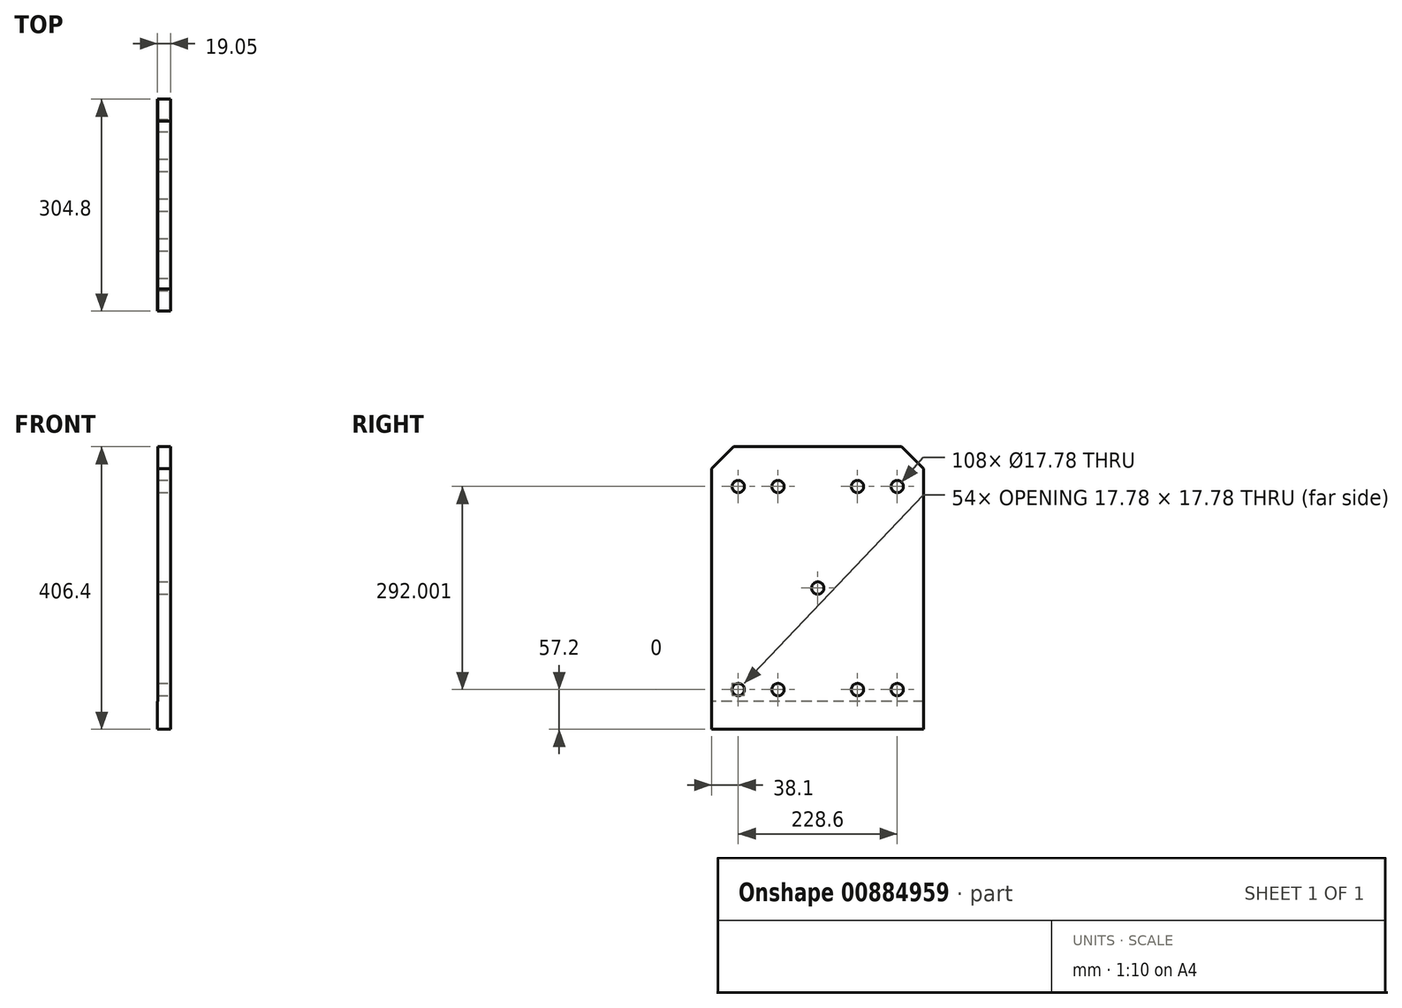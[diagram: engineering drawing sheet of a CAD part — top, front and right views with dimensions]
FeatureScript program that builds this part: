
annotation { "Feature Type Name" : "Feature", "Feature Type Description" : "" }
export const myFeature = defineFeature(function(context is Context, id is Id, definition is map)
    precondition{}
    {
        {
            var Q0;
            Q0=qCreatedBy(makeId("Right.planeOp"),FACE);
            var sketch = newSketch(context, id + "F0", { "sketchPlane" : qUnion([Q0])});
            skLineSegment(sketch, "E0.bottom", {"start": v(152.4, -203.2) * mm, "end": v(-152.4, -203.2) * mm});
            skLineSegment(sketch, "E0.top", {"start": v(120.65, 203.2) * mm, "end": v(-120.65, 203.2) * mm});
            skLineSegment(sketch, "E0.left", {"start": v(152.4, -203.2) * mm, "end": v(152.4, 171.45) * mm});
            skLineSegment(sketch, "E0.right", {"start": v(-152.4, -203.2) * mm, "end": v(-152.4, 171.45) * mm});
            skPoint(sketch, "E0.middle", {"position": v(0, 0) * mm});
            skPoint(sketch, "E1", {"position": v(152.4, 171.45) * mm});
            skLineSegment(sketch, "E2", {"start": v(152.4, 171.45) * mm, "end": v(120.65, 203.2) * mm});
            skPoint(sketch, "E3.orphan", {"position": v(152.4, 203.2) * mm});
            skLineSegment(sketch, "E4", {"start": v(152.4, 171.45) * mm, "end": v(-152.4, 171.45) * mm, "construction": true});
            skLineSegment(sketch, "E5", {"start": v(-152.4, 171.45) * mm, "end": v(-120.65, 203.2) * mm});
            skPoint(sketch, "E6.orphan", {"position": v(-152.4, 203.2) * mm});
            skSolve(sketch);
        }
        {
            var Q0;
            Q0 = qSketchRegion(id + "F0", true);
            extrude(context, id + "F1", {"entities" : qUnion([Q0]), "depth" : 19.05 * mm, "offsetDistance" : 25.4 * mm});
        }
        {
            var Q0;
            Q0=makeQuery(id+"F1.opExtrude","CAP_FACE",FACE,{"disambiguationData":[OSD([sQuery(id+"F0.wireOp",EDGE,"E0.bottom"),sQuery(id+"F0.wireOp",EDGE,"E0.top"),sQuery(id+"F0.wireOp",EDGE,"E0.left"),sQuery(id+"F0.wireOp",EDGE,"E0.right"),sQuery(id+"F0.wireOp",EDGE,"E2"),sQuery(id+"F0.wireOp",EDGE,"E5")])],"isStart":false});
            var sketch = newSketch(context, id + "F2", { "sketchPlane" : qUnion([Q0])});
            skLineSegment(sketch, "E7", {"start": v(0, -203.2) * mm, "end": v(0, 203.2) * mm, "construction": true});
            skPoint(sketch, "E8", {"position": v(0, -186.84) * mm});
            skCircle(sketch, "E9", {"center": v(-57.15, 146) * mm, "radius": 8.9 * mm});
            skCircle(sketch, "E10", {"center": v(-114.3, 146) * mm, "radius": 8.9 * mm});
            skCircle(sketch, "E11", {"center": v(0, 0) * mm, "radius": 8.9 * mm});
            skCircle(sketch, "E12", {"center": v(-57.15, -146) * mm, "radius": 8.9 * mm});
            skCircle(sketch, "E13", {"center": v(-114.3, -146) * mm, "radius": 8.9 * mm});
            skCircle(sketch, "E14.MirrorC", {"center": v(57.15, 146) * mm, "radius": 8.9 * mm});
            skCircle(sketch, "E15.MirrorC", {"center": v(114.3, 146) * mm, "radius": 8.9 * mm});
            skCircle(sketch, "E16.MirrorC", {"center": v(57.15, -146) * mm, "radius": 8.9 * mm});
            skCircle(sketch, "E17.MirrorC", {"center": v(114.3, -146) * mm, "radius": 8.9 * mm});
            skPoint(sketch, "E18.center.orphan", {"position": v(-38.1, 130.66) * mm});
            skSolve(sketch);
        }
        {
            var Q0;
            Q0 = qSketchRegion(id + "F2", true);
            extrude(context, id + "F3", {"entities" : qUnion([Q0]), "operationType" : NewBodyOperationType.REMOVE, "oppositeDirection" : true, "depth" : 96.01 * mm, "offsetDistance" : 25.4 * mm});
        }
        {
            var Q0;
            Q0=makeQuery(id+"F1.opExtrude","CAP_FACE",FACE,{"disambiguationData":[OSD([sQuery(id+"F0.wireOp",EDGE,"E0.bottom"),sQuery(id+"F0.wireOp",EDGE,"E0.top"),sQuery(id+"F0.wireOp",EDGE,"E0.left"),sQuery(id+"F0.wireOp",EDGE,"E0.right"),sQuery(id+"F0.wireOp",EDGE,"E2"),sQuery(id+"F0.wireOp",EDGE,"E5")])],"isStart":true});
            var sketch = newSketch(context, id + "F4", { "sketchPlane" : qUnion([Q0])});
            skLineSegment(sketch, "E19.bottom", {"start": v(-152.4, 203.2) * mm, "end": v(152.4, 203.2) * mm});
            skLineSegment(sketch, "E19.top", {"start": v(-152.4, -163.14) * mm, "end": v(152.4, -163.14) * mm});
            skLineSegment(sketch, "E19.left", {"start": v(-152.4, 203.2) * mm, "end": v(-152.4, -163.14) * mm});
            skLineSegment(sketch, "E19.right", {"start": v(152.4, 203.2) * mm, "end": v(152.4, -163.14) * mm});
            skSolve(sketch);
        }
        {
            var Q0;
            Q0 = qSketchRegion(id + "F4", true);
            extrude(context, id + "F5", {"entities" : qUnion([Q0]), "operationType" : NewBodyOperationType.REMOVE, "oppositeDirection" : true, "depth" : 0.5 * mm, "offsetDistance" : 25.4 * mm});
        }
    });
